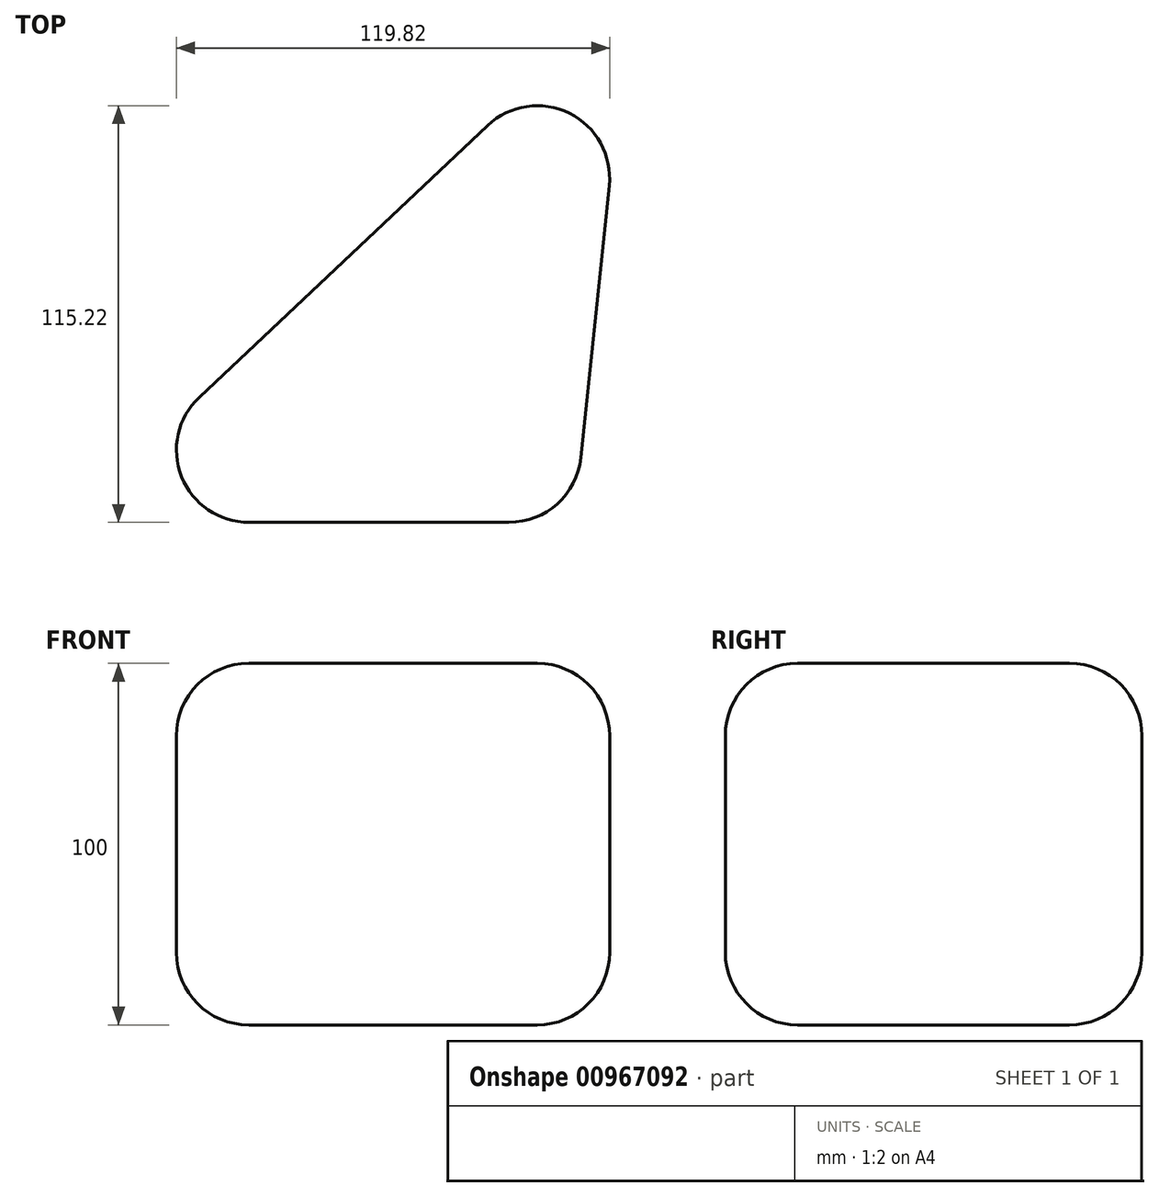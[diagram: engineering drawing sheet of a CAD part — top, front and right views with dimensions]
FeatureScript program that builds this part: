
annotation { "Feature Type Name" : "Feature", "Feature Type Description" : "" }
export const myFeature = defineFeature(function(context is Context, id is Id, definition is map)
    precondition{}
    {
        {
            var Q0;
            Q0=qCreatedBy(makeId("Top.planeOp"),FACE);
            var sketch = newSketch(context, id + "F0", { "sketchPlane" : qUnion([Q0])});
            skLineSegment(sketch, "E0", {"start": v(80.7, 81.91) * mm, "end": v(-74.98, -64.8) * mm});
            skLineSegment(sketch, "E1", {"start": v(-74.98, -64.8) * mm, "end": v(-74.98, -64.8) * mm});
            skLineSegment(sketch, "E2", {"start": v(-68.14, -58.36) * mm, "end": v(-74.98, -51.1) * mm});
            skLineSegment(sketch, "E3", {"start": v(-74.98, -51.1) * mm, "end": v(-74.98, -64.8) * mm});
            skLineSegment(sketch, "E4", {"start": v(-74.98, -64.8) * mm, "end": v(65.41, -64.8) * mm});
            skLineSegment(sketch, "E5", {"start": v(65.41, -64.8) * mm, "end": v(80.7, 81.91) * mm});
            skSolve(sketch);
        }
        {
            var Q0;
            {var subQ3=sQuery(id+"F0.wireOp",EDGE,"E4");Q0=makeQuery(id+"F0.imprint","IMPRINT",FACE,{"disambiguationData":[TD([[makeQuery(id+"F0.imprint","IMPRINT",EDGE,{"derivedFrom":subQ3}),1.0]])]});}
            extrude(context, id + "F1", {"entities" : qUnion([Q0]), "depth" : 100 * mm, "offsetDistance" : 25.4 * mm});
        }
        {
            var Q0;
            Q0=makeQuery(id+"F1.opExtrude","CAP_FACE",FACE,{"disambiguationData":[OSD([sQuery(id+"F0.wireOp",EDGE,"E0"),sQuery(id+"F0.wireOp",EDGE,"E4"),sQuery(id+"F0.wireOp",EDGE,"E5")])],"isStart":false});
            var Q1;
            Q1=makeQuery(id+"F1.opExtrude","CAP_EDGE",EDGE,{"disambiguationData":[OSD([sQuery(id+"F0.wireOp",EDGE,"E5")])],"isStart":false});
            var Q2;
            Q2=makeQuery(id+"F1.opExtrude","SWEPT_FACE",FACE,{"disambiguationData":[OSD([sQuery(id+"F0.wireOp",EDGE,"E5")])]});
            var Q3;
            Q3=makeQuery(id+"F1.opExtrude","SWEPT_FACE",FACE,{"disambiguationData":[OSD([sQuery(id+"F0.wireOp",EDGE,"E4")])]});
            var Q4;
            Q4=makeQuery(id+"F1.opExtrude","CAP_FACE",FACE,{"disambiguationData":[OSD([sQuery(id+"F0.wireOp",EDGE,"E0"),sQuery(id+"F0.wireOp",EDGE,"E4"),sQuery(id+"F0.wireOp",EDGE,"E5")])],"isStart":true});
            fillet(context, id + "F2", {"entities" : qUnion([Q0, Q1, Q2, Q3, Q4]), "radius" : 20 * mm, "tangentPropagation" : true, "allowEdgeOverflow" : false});
        }
    });
